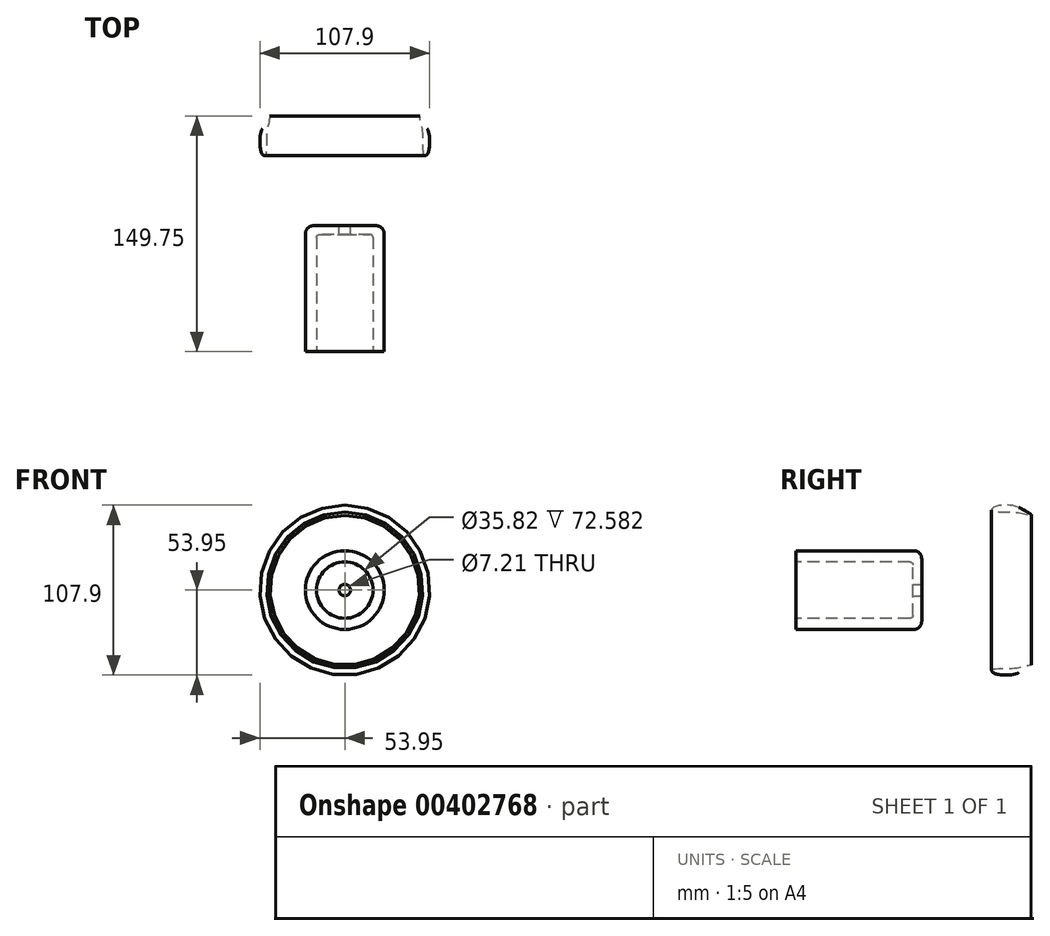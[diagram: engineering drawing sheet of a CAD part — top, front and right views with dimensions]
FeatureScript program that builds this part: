
annotation { "Feature Type Name" : "Feature", "Feature Type Description" : "" }
export const myFeature = defineFeature(function(context is Context, id is Id, definition is map)
    precondition{}
    {
        {
            var Q0;
            Q0=qCreatedBy(makeId("Front.planeOp"),FACE);
            var sketch = newSketch(context, id + "F0", { "sketchPlane" : qUnion([Q0])});
            skCircle(sketch, "E0", {"center": v(0, 0) * mm, "radius": 25 * mm});
            skSolve(sketch);
        }
        {
            var Q0;
            Q0=makeQuery(id+"F0.imprint","IMPRINT",FACE,{"disambiguationData":[TD([[makeQuery(id+"F0.imprint","IMPRINT",EDGE,{"derivedFrom":sQuery(id+"F0.wireOp",EDGE,"E0")}),1.0]])]});
            extrude(context, id + "F1", {"entities" : qUnion([Q0]), "depth" : 80 * mm});
        }
        {
            var Q0;
            Q0=makeQuery(id+"F1.opExtrude","CAP_FACE",FACE,{"disambiguationData":[OSD([sQuery(id+"F0.wireOp",EDGE,"E0")])],"isStart":false});
            cPlane(context, id + "F2", {"entities" : qUnion([Q0]), "cplaneType" : CPlaneType.OFFSET, "offset" : 0 * mm, "width" : 152.4 * mm, "height" : 152.4 * mm});
        }
        {
            var Q0;
            Q0=qCreatedBy(makeId("Right.planeOp"),FACE);
            var sketch = newSketch(context, id + "F3", { "sketchPlane" : qUnion([Q0])});
            skFitSpline(sketch, "E1", {"points": [v(61.84, 52.35) * mm, v(54.73, 53.93) * mm, v(46.04, 52.75) * mm, v(44.46, 50.77) * mm, v(46.83, 49.98) * mm, v(53.94, 49.59) * mm, v(61.84, 49.2) * mm, v(69.75, 47.61) * mm, v(61.84, 52.35) * mm]});
            skSolve(sketch);
        }
        {
            var Q0;
            Q0=qCreatedBy(makeId("Right.planeOp"),FACE);
            var sketch = newSketch(context, id + "F4", { "sketchPlane" : qUnion([Q0])});
            skLineSegment(sketch, "E2", {"start": v(77.25, 0) * mm, "end": v(39.72, 0) * mm});
            skSolve(sketch);
        }
        {
            var Q0;
            Q0=makeQuery(id+"F3.imprint","IMPRINT",FACE,{"disambiguationData":[TD([[makeQuery(id+"F3.imprint","IMPRINT",EDGE,{"derivedFrom":sQuery(id+"F3.wireOp",EDGE,"E1")}),1.0]])]});
            var Q1;
            Q1=sQuery(id+"F4.wireOp",EDGE,"E2");
            revolve(context, id + "F5", {"entities" : qUnion([Q0]), "axis" : qUnion([Q1]), "revolveType" : RevolveType.FULL});
        }
        {
            var Q0;
            Q0=qCreatedBy(id+"F2.planeOp",FACE);
            var sketch = newSketch(context, id + "F6", { "sketchPlane" : qUnion([Q0])});
            skCircle(sketch, "E3", {"center": v(0, 0) * mm, "radius": 17.91 * mm});
            skSolve(sketch);
        }
        {
            var Q0;
            Q0=makeQuery(id+"F6.imprint","IMPRINT",FACE,{"disambiguationData":[TD([[makeQuery(id+"F6.imprint","IMPRINT",EDGE,{"derivedFrom":sQuery(id+"F6.wireOp",EDGE,"E3")}),1.0]])]});
            extrude(context, id + "F7", {"entities" : qUnion([Q0]), "operationType" : NewBodyOperationType.REMOVE, "oppositeDirection" : true, "depth" : 74.42 * mm});
        }
        {
            var Q0;
            Q0=qCreatedBy(makeId("Front.planeOp"),FACE);
            var sketch = newSketch(context, id + "F8", { "sketchPlane" : qUnion([Q0])});
            skCircle(sketch, "E4", {"center": v(0, 0) * mm, "radius": 3.6 * mm});
            skSolve(sketch);
        }
        {
            var Q0;
            Q0=makeQuery(id+"F8.imprint","IMPRINT",FACE,{"disambiguationData":[TD([[makeQuery(id+"F8.imprint","IMPRINT",EDGE,{"derivedFrom":sQuery(id+"F8.wireOp",EDGE,"E4")}),1.0]])]});
            extrude(context, id + "F9", {"entities" : qUnion([Q0]), "operationType" : NewBodyOperationType.REMOVE, "depth" : 7.62 * mm});
        }
        {
            var Q0;
            Q0=makeQuery(id+"F1.opExtrude","CAP_EDGE",EDGE,{"disambiguationData":[OSD([sQuery(id+"F0.wireOp",EDGE,"E0")])],"isStart":true});
            fillet(context, id + "F10", {"entities" : qUnion([Q0]), "radius" : 5.08 * mm, "tangentPropagation" : true, "allowEdgeOverflow" : false});
        }
        {
            var Q0;
            Q0=makeQuery(id+"F7.boolean.opBoolean","COPY",EDGE,{"derivedFrom":makeQuery(id+"F7.opExtrude","CAP_EDGE",EDGE,{"disambiguationData":[OSD([sQuery(id+"F6.wireOp",EDGE,"E3")])],"isStart":false})});
            fillet(context, id + "F11", {"entities" : qUnion([Q0]), "radius" : 1.84 * mm, "tangentPropagation" : true, "allowEdgeOverflow" : false});
        }
    });
